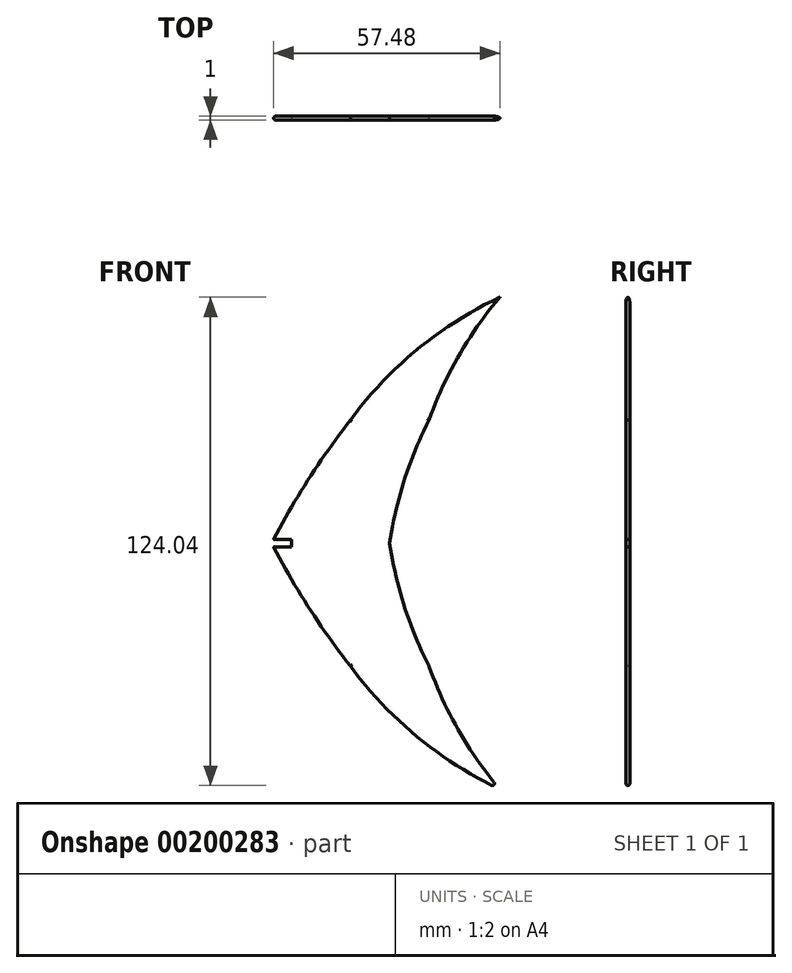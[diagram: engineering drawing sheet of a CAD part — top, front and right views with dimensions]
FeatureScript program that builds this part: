
annotation { "Feature Type Name" : "Feature", "Feature Type Description" : "" }
export const myFeature = defineFeature(function(context is Context, id is Id, definition is map)
    precondition{}
    {
        {
            var Q0;
            Q0=qCreatedBy(makeId("Front.planeOp"),FACE);
            var sketch = newSketch(context, id + "F0", { "sketchPlane" : qUnion([Q0])});
            skLineSegment(sketch, "E0", {"start": v(0, 0) * mm, "end": v(30, 0) * mm});
            skLineSegment(sketch, "E1", {"start": v(20, 31.25) * mm, "end": v(40, 31.25) * mm});
            skPoint(sketch, "E2", {"position": v(58, 62.5) * mm});
            skArc(sketch, "E3", {"start": v(20, 31.25) * mm, "mid": v(9.27, 16.09) * mm, "end": v(0, 0) * mm});
            skArc(sketch, "E4", {"start": v(58, 62.5) * mm, "mid": v(37.05, 49.25) * mm, "end": v(20, 31.25) * mm});
            skArc(sketch, "E5", {"start": v(58, 62.5) * mm, "mid": v(47.58, 47.7) * mm, "end": v(40, 31.25) * mm});
            skArc(sketch, "E6", {"start": v(40, 31.25) * mm, "mid": v(33.7, 16.04) * mm, "end": v(30, 0) * mm});
            skSolve(sketch);
        }
        {
            var Q0;
            Q0 = qSketchRegion(id + "F0", true);
            extrude(context, id + "F1", {"entities" : qUnion([Q0]), "endBound" : BoundingType.SYMMETRIC, "depth" : 1 * mm});
        }
        {
            var Q0;
            Q0=makeQuery(id+"F1.opExtrude","SWEPT_BODY",BODY,{"disambiguationData":[OSD([sQuery(id+"F0.wireOp",EDGE,"E0"),sQuery(id+"F0.wireOp",EDGE,"E3"),sQuery(id+"F0.wireOp",EDGE,"E4"),sQuery(id+"F0.wireOp",EDGE,"E5"),sQuery(id+"F0.wireOp",EDGE,"E6")])]});
            var Q1;
            Q1=qCreatedBy(makeId("Top.planeOp"),FACE);
            mirror(context, id + "F2", {"operationType" : NewBodyOperationType.ADD, "entities" : qUnion([Q0]), "mirrorPlane" : qUnion([Q1])});
        }
        {
            var Q0;
            Q0=qCreatedBy(makeId("Front.planeOp"),FACE);
            var sketch = newSketch(context, id + "F3", { "sketchPlane" : qUnion([Q0])});
            skLineSegment(sketch, "E7.bottom", {"start": v(5, -1) * mm, "end": v(-5, -1) * mm});
            skLineSegment(sketch, "E7.top", {"start": v(5, 1) * mm, "end": v(-5, 1) * mm});
            skLineSegment(sketch, "E7.left", {"start": v(5, -1) * mm, "end": v(5, 1) * mm});
            skLineSegment(sketch, "E7.right", {"start": v(-5, -1) * mm, "end": v(-5, 1) * mm});
            skPoint(sketch, "E7.middle", {"position": v(0, 0) * mm});
            skSolve(sketch);
        }
        {
            var Q0;
            Q0=makeQuery(id+"F3.imprint","IMPRINT",FACE,{"disambiguationData":[TD([[makeQuery(id+"F3.imprint","IMPRINT",EDGE,{"derivedFrom":sQuery(id+"F3.wireOp",EDGE,"E7.bottom")}),-1.0]])]});
            extrude(context, id + "F4", {"entities" : qUnion([Q0]), "operationType" : NewBodyOperationType.REMOVE, "endBound" : BoundingType.SYMMETRIC, "oppositeDirection" : true, "depth" : 5 * mm});
        }
        {
            var Q0;
            Q0=makeQuery(id+"F1.opExtrude","CAP_EDGE",EDGE,{"disambiguationData":[OSD([sQuery(id+"F0.wireOp",EDGE,"E4")])],"isStart":false});
            var Q1;
            Q1=makeQuery(id+"F1.opExtrude","CAP_EDGE",EDGE,{"disambiguationData":[OSD([sQuery(id+"F0.wireOp",EDGE,"E4")])],"isStart":true});
            var Q2;
            Q2=makeQuery(id+"F1.opExtrude","CAP_EDGE",EDGE,{"disambiguationData":[OSD([sQuery(id+"F0.wireOp",EDGE,"E3")])],"isStart":false});
            var Q3;
            Q3=makeQuery(id+"F1.opExtrude","CAP_EDGE",EDGE,{"disambiguationData":[OSD([sQuery(id+"F0.wireOp",EDGE,"E3")])],"isStart":true});
            var Q4;
            Q4=makeQuery(id+"F1.opExtrude","CAP_EDGE",EDGE,{"disambiguationData":[OSD([sQuery(id+"F0.wireOp",EDGE,"E5")])],"isStart":false});
            var Q5;
            Q5=makeQuery(id+"F1.opExtrude","CAP_EDGE",EDGE,{"disambiguationData":[OSD([sQuery(id+"F0.wireOp",EDGE,"E5")])],"isStart":true});
            var Q6;
            Q6=makeQuery(id+"F1.opExtrude","CAP_EDGE",EDGE,{"disambiguationData":[OSD([sQuery(id+"F0.wireOp",EDGE,"E6")])],"isStart":false});
            var Q7;
            Q7=makeQuery(id+"F1.opExtrude","CAP_EDGE",EDGE,{"disambiguationData":[OSD([sQuery(id+"F0.wireOp",EDGE,"E6")])],"isStart":true});
            var Q8;
            Q8=makeQuery(id+"F2.opPattern","COPY",EDGE,{"derivedFrom":makeQuery(id+"F1.opExtrude","CAP_EDGE",EDGE,{"disambiguationData":[OSD([sQuery(id+"F0.wireOp",EDGE,"E3")])],"isStart":false}),"instanceName":"1"});
            var Q9;
            Q9=makeQuery(id+"F2.opPattern","COPY",EDGE,{"derivedFrom":makeQuery(id+"F1.opExtrude","CAP_EDGE",EDGE,{"disambiguationData":[OSD([sQuery(id+"F0.wireOp",EDGE,"E3")])],"isStart":true}),"instanceName":"1"});
            var Q10;
            Q10=makeQuery(id+"F2.opPattern","COPY",EDGE,{"derivedFrom":makeQuery(id+"F1.opExtrude","CAP_EDGE",EDGE,{"disambiguationData":[OSD([sQuery(id+"F0.wireOp",EDGE,"E4")])],"isStart":false}),"instanceName":"1"});
            var Q11;
            Q11=makeQuery(id+"F2.opPattern","COPY",EDGE,{"derivedFrom":makeQuery(id+"F1.opExtrude","CAP_EDGE",EDGE,{"disambiguationData":[OSD([sQuery(id+"F0.wireOp",EDGE,"E4")])],"isStart":true}),"instanceName":"1"});
            var Q12;
            Q12=makeQuery(id+"F2.opPattern","COPY",EDGE,{"derivedFrom":makeQuery(id+"F1.opExtrude","CAP_EDGE",EDGE,{"disambiguationData":[OSD([sQuery(id+"F0.wireOp",EDGE,"E6")])],"isStart":false}),"instanceName":"1"});
            var Q13;
            Q13=makeQuery(id+"F2.opPattern","COPY",FACE,{"derivedFrom":makeQuery(id+"F1.opExtrude","SWEPT_FACE",FACE,{"disambiguationData":[OSD([sQuery(id+"F0.wireOp",EDGE,"E6")])]}),"instanceName":"1"});
            var Q14;
            Q14=makeQuery(id+"F2.opPattern","COPY",EDGE,{"derivedFrom":makeQuery(id+"F1.opExtrude","CAP_EDGE",EDGE,{"disambiguationData":[OSD([sQuery(id+"F0.wireOp",EDGE,"E5")])],"isStart":false}),"instanceName":"1"});
            var Q15;
            Q15=makeQuery(id+"F2.opPattern","COPY",FACE,{"derivedFrom":makeQuery(id+"F1.opExtrude","SWEPT_FACE",FACE,{"disambiguationData":[OSD([sQuery(id+"F0.wireOp",EDGE,"E5")])]}),"instanceName":"1"});
            fillet(context, id + "F5", {"entities" : qUnion([Q0, Q1, Q2, Q3, Q4, Q5, Q6, Q7, Q8, Q9, Q10, Q11, Q12, Q13, Q14, Q15]), "radius" : 0.5 * mm, "tangentPropagation" : true, "allowEdgeOverflow" : false});
        }
    });
